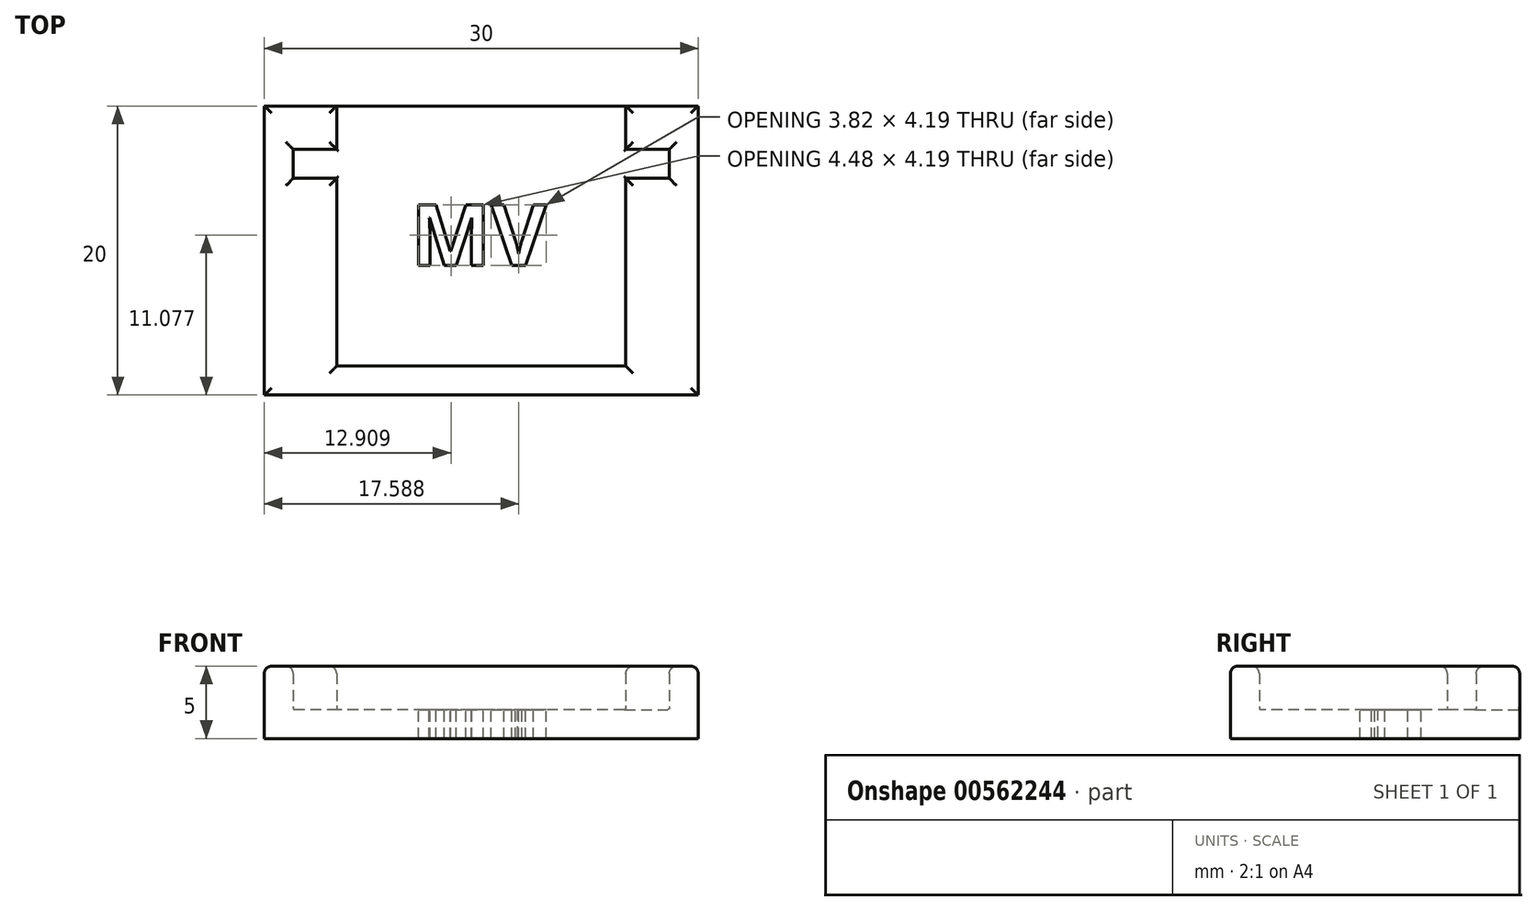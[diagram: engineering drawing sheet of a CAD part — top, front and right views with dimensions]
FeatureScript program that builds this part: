
annotation { "Feature Type Name" : "Feature", "Feature Type Description" : "" }
export const myFeature = defineFeature(function(context is Context, id is Id, definition is map)
    precondition{}
    {
        {
            var Q0;
            Q0=qCreatedBy(makeId("Top.planeOp"),FACE);
            var sketch = newSketch(context, id + "F0", { "sketchPlane" : qUnion([Q0])});
            skLineSegment(sketch, "E0", {"start": v(0, 20) * mm, "end": v(5, 20) * mm});
            skLineSegment(sketch, "E1", {"start": v(5, 20) * mm, "end": v(5, 17) * mm});
            skLineSegment(sketch, "E2", {"start": v(5, 17) * mm, "end": v(2, 17) * mm});
            skLineSegment(sketch, "E3", {"start": v(2, 17) * mm, "end": v(2, 15) * mm});
            skLineSegment(sketch, "E4", {"start": v(2, 15) * mm, "end": v(5, 15) * mm});
            skLineSegment(sketch, "E5", {"start": v(5, 15) * mm, "end": v(5, 2) * mm});
            skLineSegment(sketch, "E6", {"start": v(5, 2) * mm, "end": v(25, 2) * mm});
            skLineSegment(sketch, "E7", {"start": v(25, 2) * mm, "end": v(25, 15) * mm});
            skLineSegment(sketch, "E8", {"start": v(25, 15) * mm, "end": v(28, 15) * mm});
            skLineSegment(sketch, "E9", {"start": v(28, 15) * mm, "end": v(28, 17) * mm});
            skLineSegment(sketch, "E10", {"start": v(28, 17) * mm, "end": v(25, 17) * mm});
            skLineSegment(sketch, "E11", {"start": v(25, 17) * mm, "end": v(25, 20) * mm});
            skLineSegment(sketch, "E12", {"start": v(25, 20) * mm, "end": v(30, 20) * mm});
            skLineSegment(sketch, "E13", {"start": v(30, 20) * mm, "end": v(30, 0) * mm});
            skLineSegment(sketch, "E14", {"start": v(30, 0) * mm, "end": v(0, 0) * mm});
            skLineSegment(sketch, "E15", {"start": v(0, 0) * mm, "end": v(0, 20) * mm});
            skSolve(sketch);
        }
        {
            var Q0;
            Q0=makeQuery(id+"F0.imprint","IMPRINT",FACE,{"disambiguationData":[TD([[makeQuery(id+"F0.imprint","IMPRINT",EDGE,{"derivedFrom":sQuery(id+"F0.wireOp",EDGE,"E0")}),-1.0]])]});
            extrude(context, id + "F1", {"entities" : qUnion([Q0]), "depth" : 3 * mm, "offsetDistance" : 25 * mm});
        }
        {
            var Q0;
            Q0=makeQuery(id+"F1.opExtrude","CAP_FACE",FACE,{"disambiguationData":[OSD([sQuery(id+"F0.wireOp",EDGE,"E0"),sQuery(id+"F0.wireOp",EDGE,"E1"),sQuery(id+"F0.wireOp",EDGE,"E2"),sQuery(id+"F0.wireOp",EDGE,"E3"),sQuery(id+"F0.wireOp",EDGE,"E4"),sQuery(id+"F0.wireOp",EDGE,"E5"),sQuery(id+"F0.wireOp",EDGE,"E6"),sQuery(id+"F0.wireOp",EDGE,"E7"),sQuery(id+"F0.wireOp",EDGE,"E8"),sQuery(id+"F0.wireOp",EDGE,"E9"),sQuery(id+"F0.wireOp",EDGE,"E10"),sQuery(id+"F0.wireOp",EDGE,"E11"),sQuery(id+"F0.wireOp",EDGE,"E12"),sQuery(id+"F0.wireOp",EDGE,"E13"),sQuery(id+"F0.wireOp",EDGE,"E14"),sQuery(id+"F0.wireOp",EDGE,"E15")])],"isStart":true});
            var sketch = newSketch(context, id + "F2", { "sketchPlane" : qUnion([Q0])});
            skLineSegment(sketch, "E16.0", {"start": v(0, 0) * mm, "end": v(0, -20) * mm});
            skLineSegment(sketch, "E17.0", {"start": v(30, 0) * mm, "end": v(0, 0) * mm});
            skLineSegment(sketch, "E18.0", {"start": v(30, -20) * mm, "end": v(30, 0) * mm});
            skLineSegment(sketch, "E19", {"start": v(30, -20) * mm, "end": v(0, -20) * mm});
            skSolve(sketch);
        }
        {
            var Q0;
            {var subQ1=makeQuery(id+"F1.opExtrude","CAP_EDGE",EDGE,{"disambiguationData":[OSD([sQuery(id+"F0.wireOp",EDGE,"E1")])],"isStart":true});Q0=makeQuery(id+"F2.imprint","IMPRINT",FACE,{"disambiguationData":[TD([[makeQuery(id+"F2.imprint","IMPRINT",EDGE,{"derivedFrom":subQ1}),-1.0]])]});}
            var Q1;
            {var subQ2=sQuery(id+"F2.wireOp",EDGE,"E16.0");Q1=makeQuery(id+"F2.imprint","IMPRINT",FACE,{"disambiguationData":[TD([[makeQuery(id+"F2.imprint","IMPRINT",EDGE,{"derivedFrom":subQ2}),1.0]])]});}
            extrude(context, id + "F3", {"entities" : qUnion([Q0, Q1]), "operationType" : NewBodyOperationType.ADD, "depth" : 2 * mm, "offsetDistance" : 25 * mm});
        }
        {
            var Q0;
            Q0=makeQuery(id+"F1.opExtrude","CAP_FACE",FACE,{"disambiguationData":[OSD([sQuery(id+"F0.wireOp",EDGE,"E0"),sQuery(id+"F0.wireOp",EDGE,"E1"),sQuery(id+"F0.wireOp",EDGE,"E2"),sQuery(id+"F0.wireOp",EDGE,"E3"),sQuery(id+"F0.wireOp",EDGE,"E4"),sQuery(id+"F0.wireOp",EDGE,"E5"),sQuery(id+"F0.wireOp",EDGE,"E6"),sQuery(id+"F0.wireOp",EDGE,"E7"),sQuery(id+"F0.wireOp",EDGE,"E8"),sQuery(id+"F0.wireOp",EDGE,"E9"),sQuery(id+"F0.wireOp",EDGE,"E10"),sQuery(id+"F0.wireOp",EDGE,"E11"),sQuery(id+"F0.wireOp",EDGE,"E12"),sQuery(id+"F0.wireOp",EDGE,"E13"),sQuery(id+"F0.wireOp",EDGE,"E14"),sQuery(id+"F0.wireOp",EDGE,"E15")])],"isStart":false});
            fillet(context, id + "F4", {"entities" : qUnion([Q0]), "radius" : 0.5 * mm, "tangentPropagation" : true, "allowEdgeOverflow" : false});
        }
        {
            var Q0;
            Q0=makeQuery(id+"F3.opExtrude","CAP_FACE",FACE,{"disambiguationData":[OSD([sQuery(id+"F2.wireOp",EDGE,"E16.0"),sQuery(id+"F2.wireOp",EDGE,"E17.0"),sQuery(id+"F2.wireOp",EDGE,"E18.0"),sQuery(id+"F2.wireOp",EDGE,"E19")])],"isStart":true});
            fillet(context, id + "F5", {"entities" : qUnion([Q0]), "radius" : 0.1 * mm, "tangentPropagation" : true, "allowEdgeOverflow" : false});
        }
        {
            var Q0;
            Q0=makeQuery(id+"F3.opExtrude","CAP_FACE",FACE,{"disambiguationData":[OSD([sQuery(id+"F2.wireOp",EDGE,"E16.0"),sQuery(id+"F2.wireOp",EDGE,"E17.0"),sQuery(id+"F2.wireOp",EDGE,"E18.0"),sQuery(id+"F2.wireOp",EDGE,"E19")])],"isStart":true});
            var sketch = newSketch(context, id + "F6", { "sketchPlane" : qUnion([Q0])});
            skText(sketch, "E20", { "text": "MV", "fontName": "OpenSans-Bold.ttf"});
            skPoint(sketch, "E21", {"position": v(15, 2.1) * mm});
            const initialGuessF6  = {"E20": [0.01014, 0.00898, 1, 0, 0.00423]};
            skSetInitialGuess(sketch, initialGuessF6);
            skSolve(sketch);
        }
        {
            var Q0;
            Q0=makeQuery(id+"F6.imprint","IMPRINT",FACE,{"disambiguationData":[TD([[makeQuery(id+"F6.imprint","IMPRINT",EDGE,{"derivedFrom":sQuery(id+"F6.wireOp",EDGE,"E20.sketch_text.stroke-0")}),-1.0]])]});
            var Q1;
            Q1=makeQuery(id+"F6.imprint","IMPRINT",FACE,{"disambiguationData":[TD([[makeQuery(id+"F6.imprint","IMPRINT",EDGE,{"derivedFrom":sQuery(id+"F6.wireOp",EDGE,"E20.sketch_text.stroke-19")}),-1.0]])]});
            extrude(context, id + "F7", {"entities" : qUnion([Q0, Q1]), "operationType" : NewBodyOperationType.REMOVE, "endBound" : BoundingType.THROUGH_ALL, "oppositeDirection" : true, "depth" : 25 * mm, "offsetDistance" : 25 * mm});
        }
    });
